# Revit family: M04
name_source: partatom
category: Verbindungsmittel
units: mm (PartAtom-declared; Revit-internal decimal feet)

## family parameters
Arbeitsebenenbasiert = Nein
Beim Laden mit Abzugskörper schneiden = Nein
Gemeinsam genutzt = Nein
Immer vertikal = Nein
OmniClass-Nummer = 23.25.10.27.11.21
OmniClass-Titel = Reinforcement Couplers

## types (10) — shared parameters
Endenbearbeitung 1 = Mit Gewinde
Endenbearbeitung 2 = Mit Gewinde
Hersteller = Stahlwerk Annahütte Max Aicher GmbH Co.KG
M04_Vis = Ja
SW Winkel = 60,00°
Typenbild = M04.png
URL = http//:www.annahuette.com

## per-type parameters (varying)
| type | Außendurchmesser | Einfassung Stab 1 | Einfassung Stab 2 | Gesamtlänge | Körper | M03-Gewicht | Modell | Nenndurchmesser ø | Pos_TR2003 | Pos_TR3003 | Stabgröße 1 | Stabgröße 2 | TR2003-G | TR2003-L | TR2003-Sw | TR3003-L | TR3003-L1 | TR3003-L2 | TR3003-d | Typenkommentare | minA |
| M04-ø18 | 36 mm  [stored 0.11811 ft] | 50 mm  [stored 0.164042 ft] | 50 mm  [stored 0.164042 ft] | 175 mm  [stored 0.574147 ft] | 0,57 kg | 0,89 kg | M04=TR 3003+TR2003 | 18 mm  [stored 0.0590551 ft] | 90 mm  [stored 0.295276 ft] | 50 mm  [stored 0.164042 ft] | SAS 670 - ø18 | SAS 670 - ø18 | 0,16 kg | 40 mm  [stored 0.131234 ft] | 30 mm  [stored 0.0984252 ft] | 100 mm  [stored 0.328084 ft] | 50 mm  [stored 0.164042 ft] | 50 mm  [stored 0.164042 ft] | 36 mm  [stored 0.11811 ft] | M04-Muffenstoß | 30 mm  [stored 0.0984252 ft] |
| M04-ø22 | 40 mm  [stored 0.131234 ft] | 55 mm  [stored 0.180446 ft] | 55 mm  [stored 0.180446 ft] | 190 mm | 0,55 kg | 1,05 kg | M04=TR 3003+TR2003 | 22 mm  [stored 0.0721785 ft] | 100 mm  [stored 0.328084 ft] | 55 mm  [stored 0.180446 ft] | SAS 670 - ø22 | SAS 670 - ø22 | 0,25 kg | 45 mm  [stored 0.147638 ft] | 36 mm  [stored 0.11811 ft] | 110 mm  [stored 0.360892 ft] | 55 mm  [stored 0.180446 ft] | 55 mm  [stored 0.180446 ft] | 40 mm  [stored 0.131234 ft] | M04-Muffenstoß | 35 mm  [stored 0.114829 ft] |
| M04-ø25 | 45 mm  [stored 0.147638 ft] | 65 mm  [stored 0.213255 ft] | 65 mm  [stored 0.213255 ft] | 205 mm  [stored 0.672572 ft] | 1,05 kg | 1,79 kg | M04=TR 3003+TR2003 | 25 mm  [stored 0.082021 ft] | 115 mm  [stored 0.377297 ft] | 65 mm  [stored 0.213255 ft] | SAS 670 - ø25 | SAS 670 - ø25 | 0,37 kg | 50 mm  [stored 0.164042 ft] | 41 mm  [stored 0.134514 ft] | 130 mm  [stored 0.426509 ft] | 65 mm  [stored 0.213255 ft] | 65 mm  [stored 0.213255 ft] | 45 mm  [stored 0.147638 ft] | M04-Muffenstoß | 40 mm  [stored 0.131234 ft] |
| M04-ø28 | 50 mm  [stored 0.164042 ft] | 70 mm  [stored 0.229659 ft] | 70 mm  [stored 0.229659 ft] | 225 mm | 1,36 kg | 2,36 kg | M04=TR 3003+TR2003 | 28 mm  [stored 0.0918635 ft] | 125 mm  [stored 0.410105 ft] | 70 mm  [stored 0.229659 ft] | SAS 670 - ø28 | SAS 670 - ø28 | 0,50 kg | 55 mm  [stored 0.180446 ft] | 46 mm  [stored 0.150919 ft] | 140 mm  [stored 0.459318 ft] | 70 mm  [stored 0.229659 ft] | 70 mm  [stored 0.229659 ft] | 50 mm  [stored 0.164042 ft] | M04-Muffenstoß | 45 mm  [stored 0.147638 ft] |
| M04-ø30 | 55 mm  [stored 0.180446 ft] | 75 mm | 75 mm | 260 mm | 1,84 kg | 3,18 kg | M04=TR 3003+TR2003 | 30 mm  [stored 0.0984252 ft] | 135 mm  [stored 0.442913 ft] | 75 mm | SAS 670 - ø30 | SAS 670 - ø30 | 0,67 kg | 60 mm  [stored 0.19685 ft] | 50 mm  [stored 0.164042 ft] | 150 mm | 75 mm | 75 mm | 55 mm  [stored 0.180446 ft] | M04-Muffenstoß | 50 mm  [stored 0.164042 ft] |
| M04-ø35 | 65 mm  [stored 0.213255 ft] | 90 mm  [stored 0.295276 ft] | 90 mm  [stored 0.295276 ft] | 275 mm | 3,16 kg | 4,72 kg | M04=TR 3003+TR2003 | 35 mm  [stored 0.114829 ft] | 155 mm  [stored 0.50853 ft] | 90 mm  [stored 0.295276 ft] | SAS 670 - ø35 | SAS 670 - ø35 | 0,78 kg | 65 mm  [stored 0.213255 ft] | 55 mm  [stored 0.180446 ft] | 180 mm  [stored 0.590551 ft] | 90 mm  [stored 0.295276 ft] | 90 mm  [stored 0.295276 ft] | 65 mm  [stored 0.213255 ft] | M04-Muffenstoß | 55 mm  [stored 0.180446 ft] |
| M04-ø43 | 80 mm  [stored 0.262467 ft] | 100 mm  [stored 0.328084 ft] | 100 mm  [stored 0.328084 ft] | 335 mm | 5,42 kg | 8,62 kg | M04=TR3003+TR2003 | 43 mm  [stored 0.141076 ft] | 180 mm  [stored 0.590551 ft] | 100 mm  [stored 0.328084 ft] | SAS 670 - ø43 | SAS 670 - ø43 | 1,60 kg | 80 mm  [stored 0.262467 ft] | 70 mm  [stored 0.229659 ft] | 200 mm  [stored 0.656168 ft] | 100 mm  [stored 0.328084 ft] | 100 mm  [stored 0.328084 ft] | 80 mm  [stored 0.262467 ft] | M04-Muffenstoß | 60 mm  [stored 0.19685 ft] |
| M04-ø50 | 90 mm  [stored 0.295276 ft] | 105 mm  [stored 0.344488 ft] | 105 mm  [stored 0.344488 ft] | 350 mm | 6,92 kg | 11,46 kg | M04=TR 3003+TR2003 | 50 mm  [stored 0.164042 ft] | 195 mm  [stored 0.639764 ft] | 105 mm  [stored 0.344488 ft] | SAS 670 - ø50 | SAS 670 - ø50 | 2,27 kg | 90 mm  [stored 0.295276 ft] | 80 mm  [stored 0.262467 ft] | 210 mm  [stored 0.688976 ft] | 105 mm  [stored 0.344488 ft] | 105 mm  [stored 0.344488 ft] | 90 mm  [stored 0.295276 ft] | M04-Muffenstoß | 75 mm |
| M04-ø57,5 | 102 mm | 125 mm  [stored 0.410105 ft] | 125 mm  [stored 0.410105 ft] | 405 mm | 10,37 kg | 17,79 kg | M04=TR 3003+TR2003 | 58 mm | 225 mm | 125 mm  [stored 0.410105 ft] | SAS 670 - ø57,5 | SAS 670 - ø57,5 | 3,71 kg | 100 mm  [stored 0.328084 ft] | 90 mm  [stored 0.295276 ft] | 250 mm | 125 mm  [stored 0.410105 ft] | 125 mm  [stored 0.410105 ft] | 102 mm | M04-Muffenstoß | 75 mm |
| M04-ø63,5 | 114 mm  [stored 0.374016 ft] | 150 mm | 150 mm | 425 mm | 15,85 kg | 26,75 kg | M04=TR 3015+TR2003 | 43 mm  [stored 0.141076 ft] | 265 mm | 150 mm | SAS 670 - ø63,5 | SAS 670 - ø63,5 | 5,45 kg | 115 mm  [stored 0.377297 ft] | 100 mm  [stored 0.328084 ft] | 300 mm | 150 mm | 150 mm | 114 mm  [stored 0.374016 ft] | M04 - Muffenstoß | 80 mm  [stored 0.262467 ft] |

note: column(s) folded — value = type name in every type: Beschreibung

note: [stored X ft] marks values corroborated as IEEE doubles in the binary element streams (Revit-internal decimal feet)
